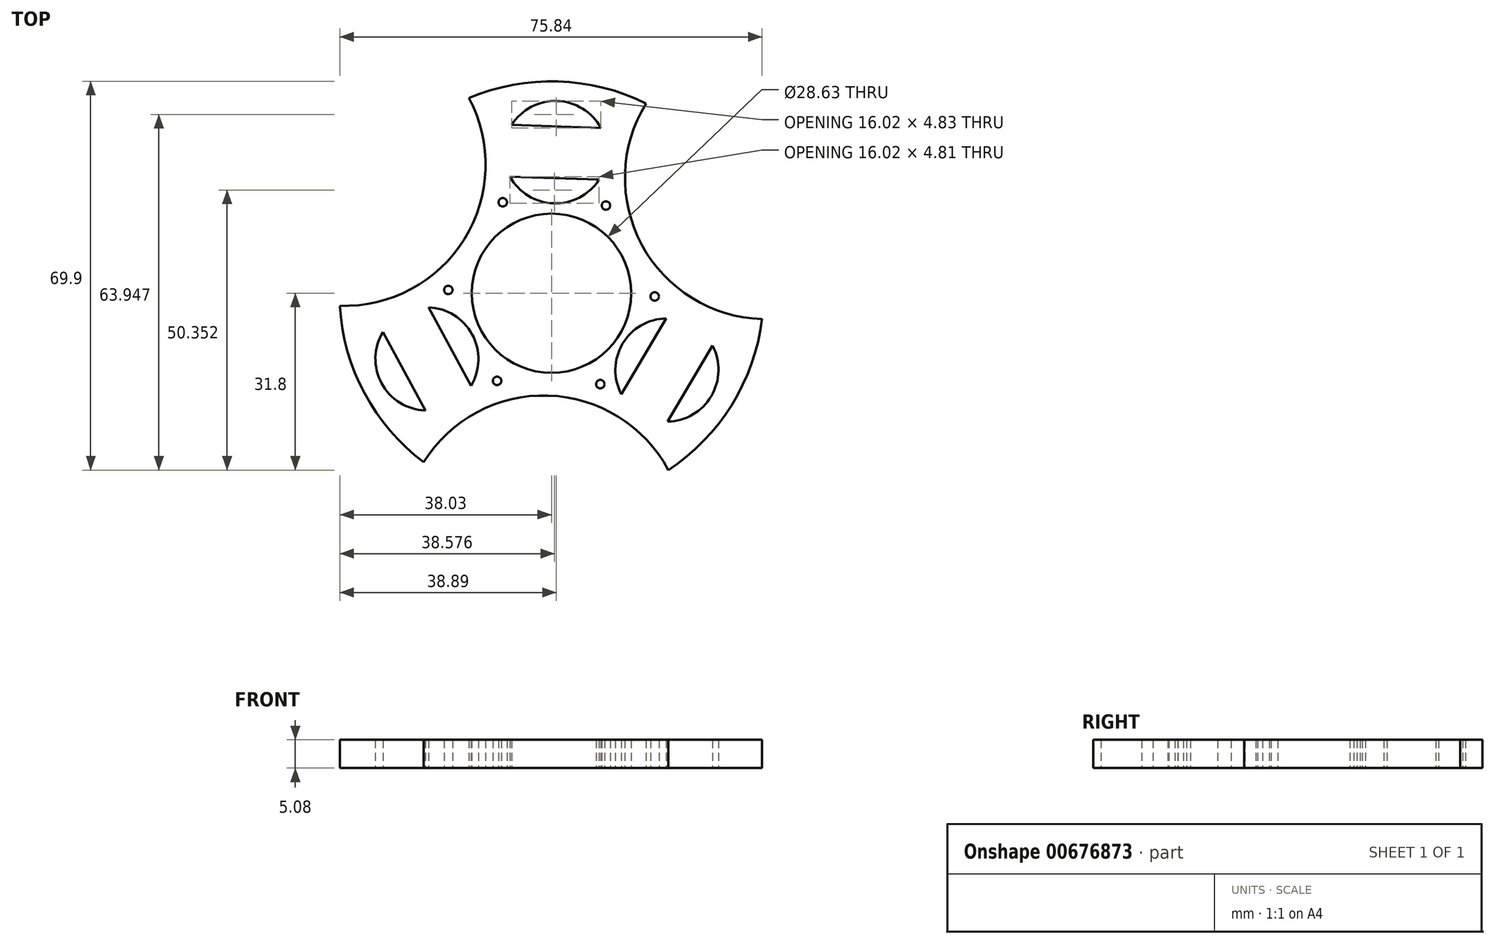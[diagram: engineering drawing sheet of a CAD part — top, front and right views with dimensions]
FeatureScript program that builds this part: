
annotation { "Feature Type Name" : "Feature", "Feature Type Description" : "" }
export const myFeature = defineFeature(function(context is Context, id is Id, definition is map)
    precondition{}
    {
        {
            var Q0;
            Q0=qCreatedBy(makeId("Top.planeOp"),FACE);
            var sketch = newSketch(context, id + "F0", { "sketchPlane" : qUnion([Q0])});
            skCircle(sketch, "E0.cCircle", {"center": v(0, 0) * mm, "radius": 38.1 * mm});
            skPoint(sketch, "E0.0.midPoint", {"position": v(-32.38, 20.08) * mm});
            skLineSegment(sketch, "E1", {"start": v(-43.96, 1.34) * mm, "end": v(20.02, 35.73) * mm, "construction": true});
            skLineSegment(sketch, "E2", {"start": v(21.09, -38.3) * mm, "end": v(20.02, 35.73) * mm, "construction": true});
            skLineSegment(sketch, "E3", {"start": v(21.09, -38.3) * mm, "end": v(-30.3, -6.99) * mm, "construction": true});
            skLineSegment(sketch, "E4", {"start": v(-20.75, 38.8) * mm, "end": v(-22.08, -2.55) * mm, "construction": true});
            skLineSegment(sketch, "E5", {"start": v(43.57, -1.57) * mm, "end": v(-23.2, -37.35) * mm, "construction": true});
            skLineSegment(sketch, "E6", {"start": v(-20.75, 38.8) * mm, "end": v(43.57, -1.57) * mm, "construction": true});
            skCircle(sketch, "E7", {"center": v(0, 0) * mm, "radius": 14.31 * mm});
            skArc(sketch, "E8", {"start": v(-38.03, -2.27) * mm, "mid": v(-15.65, 9.72) * mm, "end": v(-14.83, 35.1) * mm});
            skArc(sketch, "E9", {"start": v(17, 34.1) * mm, "mid": v(16.22, 8.71) * mm, "end": v(37.81, -4.65) * mm});
            skArc(sketch, "E10", {"start": v(21, -31.8) * mm, "mid": v(-0.59, -18.4) * mm, "end": v(-22.97, -30.4) * mm});
            skLineSegment(sketch, "E11", {"start": v(20.6, -4.54) * mm, "end": v(12.56, -18.19) * mm});
            skLineSegment(sketch, "E12", {"start": v(28.9, -9.43) * mm, "end": v(20.87, -23.08) * mm});
            skLineSegment(sketch, "E13", {"start": v(-7.46, 20.96) * mm, "end": v(8.55, 20.42) * mm});
            skLineSegment(sketch, "E14", {"start": v(-7.15, 30.27) * mm, "end": v(8.87, 29.73) * mm});
            skLineSegment(sketch, "E15", {"start": v(-30.3, -6.99) * mm, "end": v(-43.96, 1.34) * mm, "construction": true});
            skLineSegment(sketch, "E16", {"start": v(-30.3, -6.99) * mm, "end": v(-30.3, -6.99) * mm});
            skLineSegment(sketch, "E17", {"start": v(-22.08, -2.55) * mm, "end": v(-22.08, -2.55) * mm});
            skLineSegment(sketch, "E18", {"start": v(-22.08, -2.55) * mm, "end": v(-23.2, -37.35) * mm, "construction": true});
            skArc(sketch, "E19", {"start": v(-30.3, -6.99) * mm, "mid": v(-30.51, -16.21) * mm, "end": v(-22.67, -21.08) * mm});
            skArc(sketch, "E20", {"start": v(-14.46, -16.64) * mm, "mid": v(-14.25, -7.42) * mm, "end": v(-22.08, -2.55) * mm});
            skLineSegment(sketch, "E21", {"start": v(-30.3, -6.99) * mm, "end": v(-22.67, -21.08) * mm});
            skLineSegment(sketch, "E22", {"start": v(-22.08, -2.55) * mm, "end": v(-14.46, -16.64) * mm});
            skArc(sketch, "E23", {"start": v(20.6, -4.54) * mm, "mid": v(12.76, -9.1) * mm, "end": v(12.56, -18.19) * mm});
            skArc(sketch, "E24", {"start": v(20.87, -23.08) * mm, "mid": v(28.7, -18.5) * mm, "end": v(28.9, -9.43) * mm});
            skArc(sketch, "E25", {"start": v(8.87, 29.73) * mm, "mid": v(1.01, 34.56) * mm, "end": v(-7.15, 30.27) * mm});
            skArc(sketch, "E26", {"start": v(-7.46, 20.96) * mm, "mid": v(0.4, 16.15) * mm, "end": v(8.55, 20.42) * mm});
            skCircle(sketch, "E27.cCircle", {"center": v(0, 0) * mm, "radius": 16.06 * mm, "construction": true});
            skPoint(sketch, "E27.0.midPoint", {"position": v(-14.16, -7.59) * mm});
            skCircle(sketch, "E28", {"center": v(-8.76, 16.35) * mm, "radius": 0.76 * mm});
            skCircle(sketch, "E29", {"center": v(9.78, 15.76) * mm, "radius": 0.76 * mm});
            skCircle(sketch, "E30", {"center": v(18.54, -0.59) * mm, "radius": 0.76 * mm});
            skCircle(sketch, "E31", {"center": v(8.76, -16.35) * mm, "radius": 0.76 * mm});
            skCircle(sketch, "E32", {"center": v(-9.78, -15.76) * mm, "radius": 0.76 * mm});
            skCircle(sketch, "E33", {"center": v(-18.54, 0.59) * mm, "radius": 0.76 * mm});
            skSolve(sketch);
        }
        {
            var Q0;
            Q0=makeQuery(id+"F0.imprint","IMPRINT",FACE,{"disambiguationData":[TD([[makeQuery(id+"F0.imprint","IMPRINT",EDGE,{"derivedFrom":sQuery(id+"F0.wireOp",EDGE,"E7")}),-1.0]])]});
            extrude(context, id + "F1", {"entities" : qUnion([Q0]), "depth" : 5.08 * mm, "offsetDistance" : 25.4 * mm});
        }
    });
